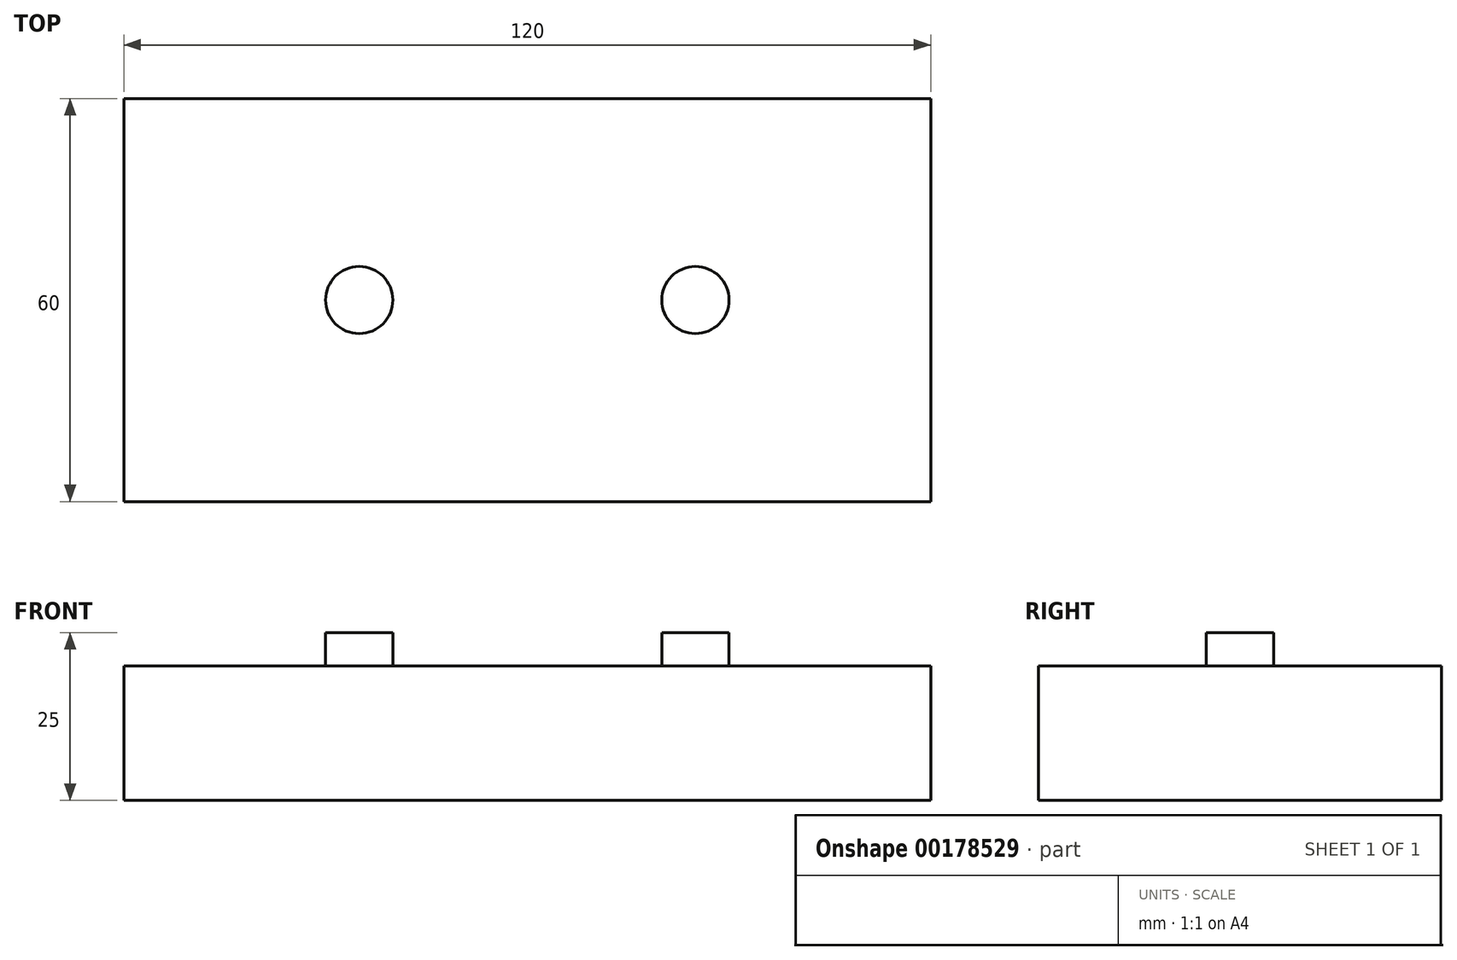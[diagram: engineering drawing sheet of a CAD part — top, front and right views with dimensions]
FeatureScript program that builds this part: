
annotation { "Feature Type Name" : "Feature", "Feature Type Description" : "" }
export const myFeature = defineFeature(function(context is Context, id is Id, definition is map)
    precondition{}
    {
        {
            var Q0;
            Q0=qCreatedBy(makeId("Top.planeOp"),FACE);
            var sketch = newSketch(context, id + "F0", { "sketchPlane" : qUnion([Q0])});
            skLineSegment(sketch, "E0.bottom", {"start": v(-60, 30) * mm, "end": v(60, 30) * mm});
            skLineSegment(sketch, "E0.top", {"start": v(-60, -30) * mm, "end": v(60, -30) * mm});
            skLineSegment(sketch, "E0.left", {"start": v(-60, 30) * mm, "end": v(-60, -30) * mm});
            skLineSegment(sketch, "E0.right", {"start": v(60, 30) * mm, "end": v(60, -30) * mm});
            skSolve(sketch);
        }
        {
            var Q0;
            Q0=makeQuery(id+"F0.imprint","IMPRINT",FACE,{"disambiguationData":[TD([[makeQuery(id+"F0.imprint","IMPRINT",EDGE,{"derivedFrom":sQuery(id+"F0.wireOp",EDGE,"E0.bottom")}),-1.0]])]});
            extrude(context, id + "F1", {"entities" : qUnion([Q0]), "depth" : 20 * mm});
        }
        {
            var Q0;
            Q0=makeQuery(id+"F1.opExtrude","CAP_FACE",FACE,{"disambiguationData":[OSD([sQuery(id+"F0.wireOp",EDGE,"E0.bottom"),sQuery(id+"F0.wireOp",EDGE,"E0.top"),sQuery(id+"F0.wireOp",EDGE,"E0.left"),sQuery(id+"F0.wireOp",EDGE,"E0.right")])],"isStart":false});
            var sketch = newSketch(context, id + "F2", { "sketchPlane" : qUnion([Q0])});
            skCircle(sketch, "E1", {"center": v(25, 0) * mm, "radius": 5 * mm});
            skCircle(sketch, "E2", {"center": v(-25, 0) * mm, "radius": 5 * mm});
            skSolve(sketch);
        }
        {
            var Q0;
            Q0 = qSketchRegion(id + "F2", true);
            extrude(context, id + "F3", {"entities" : qUnion([Q0]), "operationType" : NewBodyOperationType.ADD, "depth" : 5 * mm});
        }
    });
